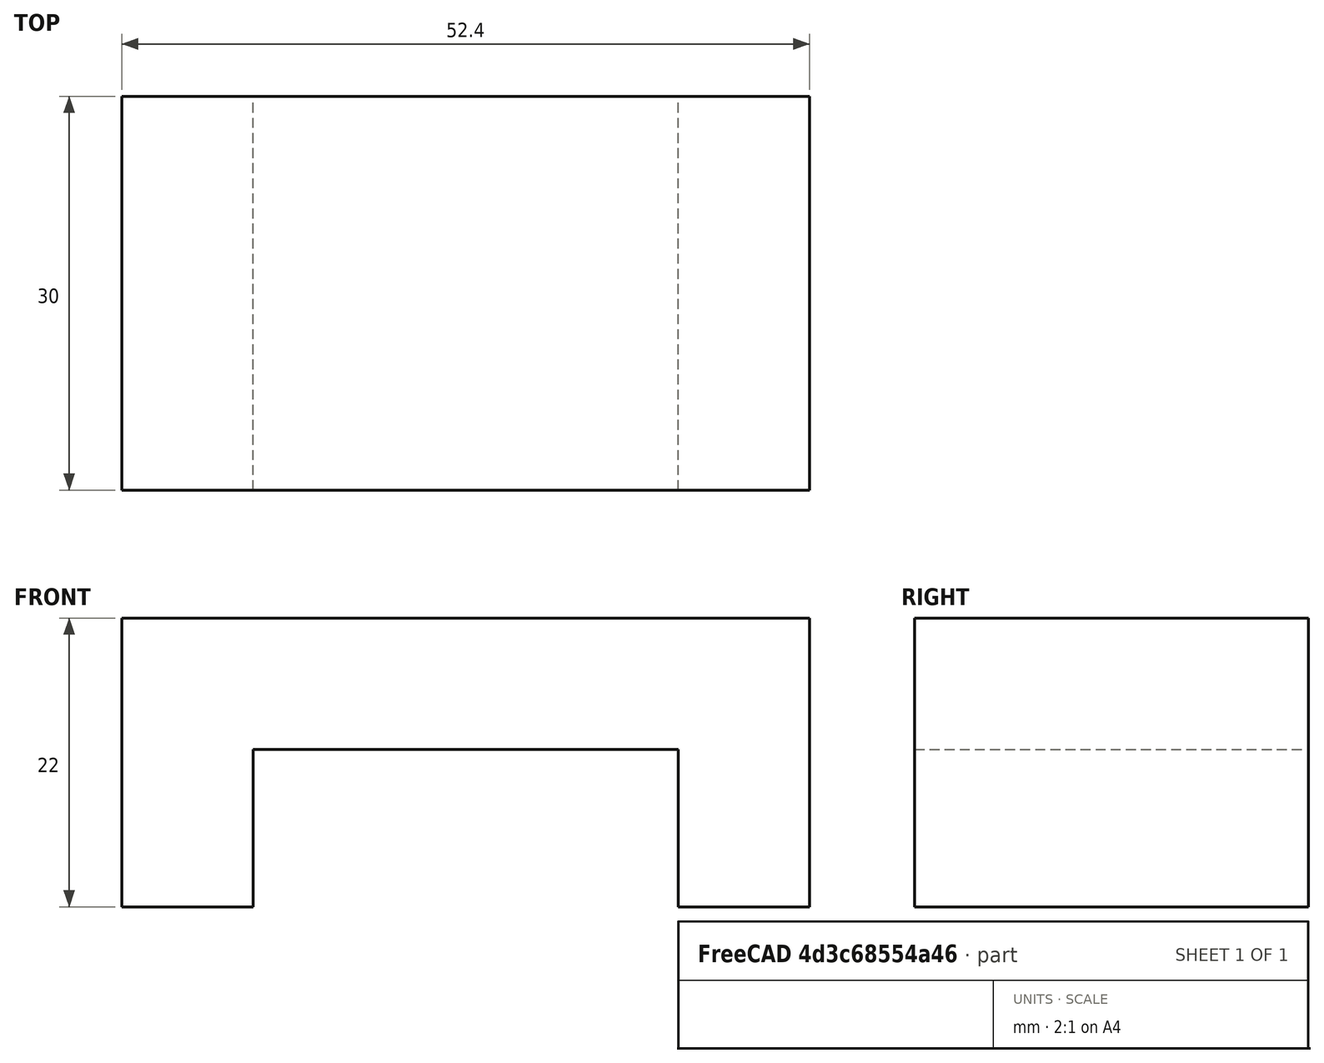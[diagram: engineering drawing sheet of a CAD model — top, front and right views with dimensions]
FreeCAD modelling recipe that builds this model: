
FCSTD DOCUMENT  (FreeCAD 0.15R4669 (Git))
Label: BR_archeBillePorteuse
License: All rights reserved
LicenseURL: http://en.wikipedia.org/wiki/All_rights_reserved
objects: Sketcher::SketchObject×1, Part::Extrusion×1
note: 2 computed .brp shape members not serialized (recipe doc carries the construction recipe); baked Part::Feature solids carry a one-line shape summary decoded from their .brp

FEATURE [Sketcher::SketchObject] Sketch
  Placement = pos=(0,0,0) rot=(-1,0,0;4.71239rad)
  sketch-geometry (8):
    g0: LineSegment StartX=-26.2 StartY=22 StartZ=0 EndX=26.2 EndY=22 EndZ=0
    g1: LineSegment StartX=26.2 StartY=22 StartZ=0 EndX=26.2 EndY=0 EndZ=0
    g2: LineSegment StartX=26.2 StartY=0 StartZ=0 EndX=16.2 EndY=0 EndZ=0
    g3: LineSegment StartX=16.2 StartY=0 StartZ=0 EndX=16.2 EndY=12 EndZ=0
    g4: LineSegment StartX=16.2 StartY=12 StartZ=0 EndX=-16.2 EndY=12 EndZ=0
    g5: LineSegment StartX=-16.2 StartY=12 StartZ=0 EndX=-16.2 EndY=0 EndZ=0
    g6: LineSegment StartX=-16.2 StartY=0 StartZ=0 EndX=-26.2 EndY=0 EndZ=0
    g7: LineSegment StartX=-26.2 StartY=0 StartZ=0 EndX=-26.2 EndY=22 EndZ=0
  constraints (25):
    c: Horizontal(g0)
    c: Coincident(g0,g1)
    c: Vertical(g1)
    c: Coincident(g1,g2)
    c: Horizontal(g2)
    c: Coincident(g2,g3)
    c: Vertical(g3)
    c: Coincident(g3,g4)
    c: Horizontal(g4)
    c: Coincident(g4,g5)
    c: Vertical(g5)
    c: Coincident(g5,g6)
    c: Horizontal(g6)
    c: Coincident(g6,g7)
    c: Vertical(g7)
    c: Coincident(g7,g0)
    c: Symmetric(g4,g3,g-2)
    c: Symmetric(g0,g0,g-2)
    c: DistanceY(g3) = 12
    c: Equal(g5,g3)
    c: DistanceY(g3,g0) = 10
    c: Equal(g6,g2)
    c: PointOnObject(g5,g-1)
    c: DistanceX(g-1,g5) = -16.2
    c: DistanceX(g6) = -10
FEATURE [Part::Extrusion] Extrude  label="archeBillePorteuse"
  Base = -> Sketch
  Dir = (0,30,0)
  Solid = true
